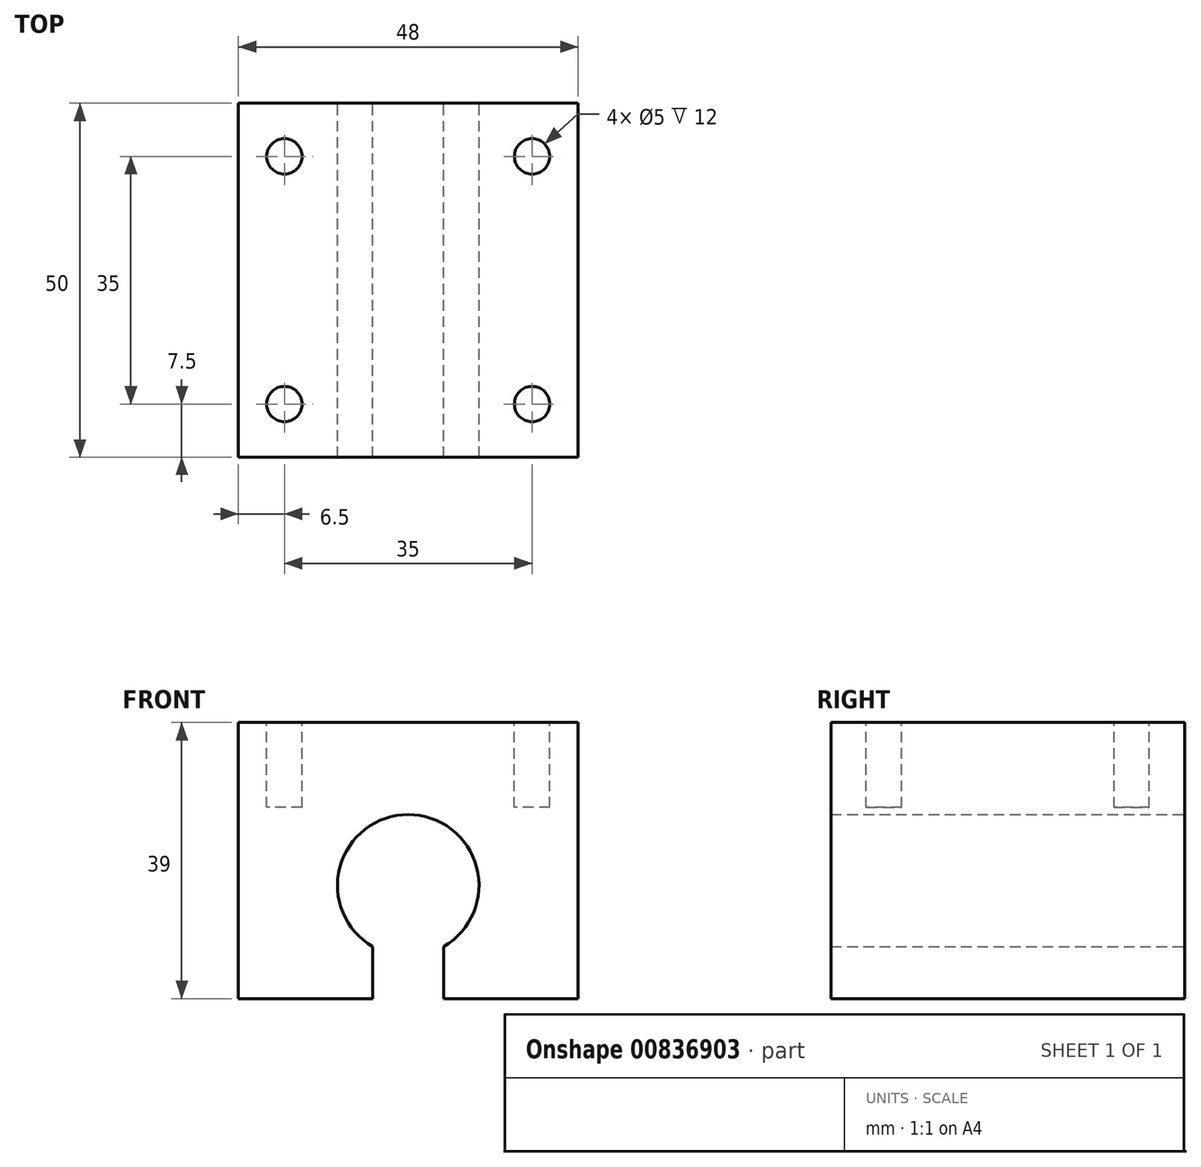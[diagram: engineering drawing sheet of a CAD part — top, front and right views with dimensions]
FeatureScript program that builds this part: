
annotation { "Feature Type Name" : "Feature", "Feature Type Description" : "" }
export const myFeature = defineFeature(function(context is Context, id is Id, definition is map)
    precondition{}
    {
        {
            var Q0;
            Q0=qCreatedBy(makeId("Front.planeOp"),FACE);
            var sketch = newSketch(context, id + "F0", { "sketchPlane" : qUnion([Q0])});
            skLineSegment(sketch, "E0.bottom", {"start": v(24, 19.5) * mm, "end": v(-24, 19.5) * mm});
            skLineSegment(sketch, "E0.top", {"start": v(24, -19.5) * mm, "end": v(5, -19.5) * mm});
            skLineSegment(sketch, "E0.left", {"start": v(24, 19.5) * mm, "end": v(24, -19.5) * mm});
            skLineSegment(sketch, "E0.right", {"start": v(-24, 19.5) * mm, "end": v(-24, -19.5) * mm});
            skPoint(sketch, "E0.middle", {"position": v(0, 0) * mm});
            skArc(sketch, "E1", {"start": v(5, -12.16) * mm, "mid": v(0, 6.5) * mm, "end": v(-5, -12.16) * mm});
            skLineSegment(sketch, "E2.left", {"start": v(5, -19.5) * mm, "end": v(5, -12.16) * mm});
            skLineSegment(sketch, "E2.right", {"start": v(-5, -19.5) * mm, "end": v(-5, -12.16) * mm});
            skPoint(sketch, "E2.middle", {"position": v(0, -19.5) * mm});
            skLineSegment(sketch, "E3.trimOffspring", {"start": v(-5, -19.5) * mm, "end": v(-24, -19.5) * mm});
            skSolve(sketch);
        }
        {
            var Q0;
            Q0 = qSketchRegion(id + "F0", true);
            extrude(context, id + "F1", {"entities" : qUnion([Q0]), "depth" : 50 * mm, "offsetDistance" : 25.4 * mm});
        }
        {
            var Q0;
            Q0=makeQuery(id+"F1.opExtrude","SWEPT_FACE",FACE,{"disambiguationData":[OSD([sQuery(id+"F0.wireOp",EDGE,"E0.bottom")])]});
            var sketch = newSketch(context, id + "F2", { "sketchPlane" : qUnion([Q0])});
            skLineSegment(sketch, "E4.bottom", {"start": v(17.5, -7.5) * mm, "end": v(-17.5, -7.5) * mm, "construction": true});
            skLineSegment(sketch, "E4.top", {"start": v(17.5, -42.5) * mm, "end": v(-17.5, -42.5) * mm, "construction": true});
            skLineSegment(sketch, "E4.left", {"start": v(17.5, -7.5) * mm, "end": v(17.5, -42.5) * mm, "construction": true});
            skLineSegment(sketch, "E4.right", {"start": v(-17.5, -7.5) * mm, "end": v(-17.5, -42.5) * mm, "construction": true});
            skPoint(sketch, "E4.middle", {"position": v(0, -25) * mm});
            skPoint(sketch, "E4.middle.positionSnap0", {"position": v(24, -25) * mm});
            skPoint(sketch, "E4.centerSnap0", {"position": v(24, -25) * mm});
            skCircle(sketch, "E5", {"center": v(-17.5, -42.5) * mm, "radius": 2.5 * mm});
            skCircle(sketch, "E6", {"center": v(-17.5, -7.5) * mm, "radius": 2.5 * mm});
            skCircle(sketch, "E7", {"center": v(17.5, -7.5) * mm, "radius": 2.5 * mm});
            skCircle(sketch, "E8", {"center": v(17.5, -42.5) * mm, "radius": 2.5 * mm});
            skSolve(sketch);
        }
        {
            var Q0;
            Q0 = qSketchRegion(id + "F2", true);
            extrude(context, id + "F3", {"entities" : qUnion([Q0]), "operationType" : NewBodyOperationType.REMOVE, "oppositeDirection" : true, "depth" : 12 * mm, "offsetDistance" : 25.4 * mm});
        }
    });
